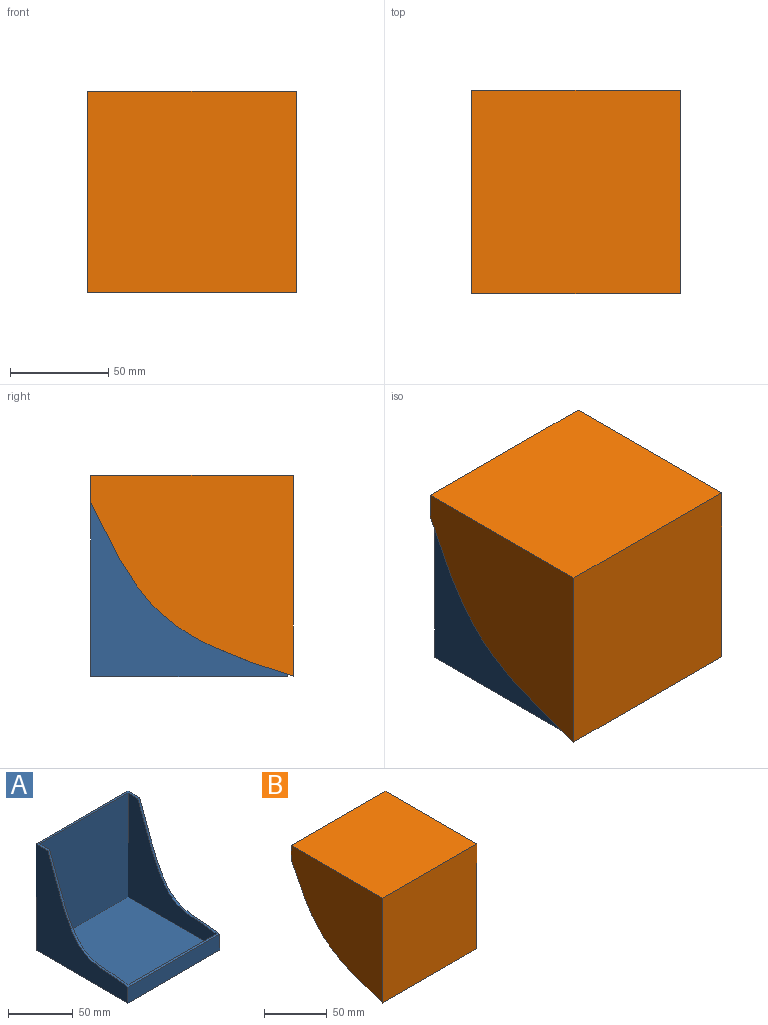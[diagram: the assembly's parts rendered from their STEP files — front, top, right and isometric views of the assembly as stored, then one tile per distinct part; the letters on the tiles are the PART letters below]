
ASSEMBLY  parts=2 mates=1
PART A: 12 faces, bbox 100x100x100 mm
  f0: plane 100x15mm, normal (0,-1,0), area 1500mm2, adj f1,f2,f3,f6
  f1: plane 100x100mm, normal (-1,0,0), area 4249.9mm2, adj f0,f2,f4,f5,f6
  f2: plane 100x100mm, normal (0,0,-1), area 10000mm2, adj f0,f1,f3,f5
  f3: plane 100x100mm, normal (1,0,0), area 4249.9mm2, adj f0,f2,f4,f5,f6
  f4: plane 100x12.57mm, normal (0,0,1), area 242.3mm2, adj f1,f3,f5,f6,f7,f9,f10
  f5: plane 100x100mm, normal (0,1,0), area 10000mm2, adj f1,f2,f3,f4
  f6: extruded ~100x87.43mm, area 740.9mm2, adj f0,f1,f3,f4,f7,f8,f9
  f7: plane 98x98mm, normal (1,0,0), area 3827.5mm2, adj f4,f6,f8,f10,f11
  f8: plane 96x13.38mm, normal (0,1,0), area 1284.2mm2, adj f6,f7,f9,f11
  f9: plane 98x98mm, normal (-1,0,0), area 3827.5mm2, adj f4,f6,f8,f10,f11
  f10: plane 98x96mm, normal (0,-1,0), area 9408mm2, adj f4,f7,f9,f11
  f11: plane 96x96mm, normal (0,0,1), area 9216mm2, adj f7,f8,f9,f10
PART B: 10 faces, bbox 106x103x102 mm
  f0: plane 106x13.56mm, normal (0,1,0), area 258.2mm2, adj f1,f2,f3,f5,f6,f7,f8
  f1: extruded ~106x103mm, area 783.5mm2, adj f0,f2,f3,f4,f7,f8,f9
  f2: plane 103x102mm, normal (1,0,0), area 7615.7mm2, adj f0,f1,f4,f5
  f3: plane 103x102mm, normal (-1,0,0), area 7615.7mm2, adj f0,f1,f4,f5
  f4: plane 106x102mm, normal (0,-1,0), area 10812mm2, adj f1,f2,f3,f5
  f5: plane 106x103mm, normal (0,0,1), area 10918mm2, adj f0,f2,f3,f4
  f6: plane 102x101mm, normal (0,0,-1), area 10302mm2, adj f0,f7,f8,f9
  f7: plane 102x100mm, normal (-1,0,0), area 7210.4mm2, adj f0,f1,f6,f9
  f8: plane 102x100mm, normal (1,0,0), area 7210.4mm2, adj f0,f1,f6,f9
  f9: plane 102x99.36mm, normal (0,1,0), area 10134.9mm2, adj f1,f6,f7,f8
PLACE A t=(9.81,-6.4,-15.03)mm
PLACE B t=(9.81,-6.4,-14.82)mm
MATE fastened B.f0 <-> A.f5  axis (0,1,0) through (9.81,43.6,84.97)mm
